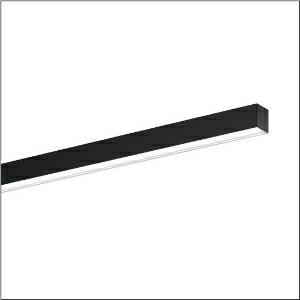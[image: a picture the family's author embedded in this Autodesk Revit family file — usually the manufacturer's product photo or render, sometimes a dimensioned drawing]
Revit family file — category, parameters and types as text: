
# Revit family: silica_r__21_51mx23tctab_c65d
name_source: partatom
category: Lighting Fixtures
units: mm (PartAtom-declared; Revit-internal decimal feet)

## family parameters
Cut with Voids When Loaded = No
Host = Face
Light Source = No
Part Type = Normal
Room Calculation Point = No
Round Connector Dimension = Use Diameter
Shared = No

## types (1)
- --- (1 x LED, 8070 lm, 81.1 W, 6500K)
    Apparent Load = 81 VA
    CIE Flux Codes = 78 96 99 100 100
    Color Rendering = 80
    Color Temperature = 6500K
    Default Elevation = 1800 mm
    Description = Silica® 21, office luminaire, primary optical cover: prismatic diffuser, of PMMA, CAT 2 (L<= 3000cd/m²), light emission: direct distribution, primary light characteristic: symmetric, installation type: surface-mounted, LED, rated luminous flux: 8.070lm, luminous efficacy: 95lm/W, light colour: 8tw, colour temperature: 2700..6500K, control gear: DALI DT8, with terminal, 3+2-pole, max. 2.5mm², mains connection: 220..240V, AC, 50/60Hz, rated input power: 85.1W, luminaire housing, of aluminium, matt jet black (RAL 9005), length: 3.004mm, width: 53mm, height: 53mm, protection rating (complete): IP20, insulation class (complete): insulation class I (protective earthing), certification: CE, permissible operating ambient temperature: 0..+35°C, standard: EN 50419, packaging unit: 1 piece
    Height = 53 mm
    Lamp = 1 x LED
    Lamp Light Flux = 8070 lm
    Lamp Power = 81.1 W
    Lamp count = 1
    Length = 3004 mm
    Luminous efficacy = 100 lm/W
    Manufacturer = Siteco
    ModVariant = No
    Model = 51MX23TCTAB
    Mounting Place = Ceiling
    Mounting Type = Surface mounted
    Number of Poles = 1
    OnlyDefault = Yes
    Power Factor = 1
    Product Name = Silica® 21
    Product group = office luminaire | ceiling mounted
    ProductGroupID = 302
    Protection Class = Protection class I
    Protection Degree = IP 20
    RLX_Detail_Level = 1
    RLX_Emergency_Light_Flux = 0 lm
    RLX_Emergency_Type = 0
    RLX_Emergency_Type_DB = No
    RlxData = <blob elided: 20369 chars, md5=80954a44>
    Socket = socket
    Standby Power = 0 W
    System Light Flux = 8070 lm
    System Power = 81 W
    Type Comments = individual setting
    Type Image = l_1335925.jpg
    URL = http://relux.com
    VarID = @adj_139806
    Voltage = 0 V
    Weight = 0.00 kg
    Width = 53 mm

## geometry (parser evidence)
native form markers: Blend x4, Sweep x11
no freeform markers — native parametric forms only
